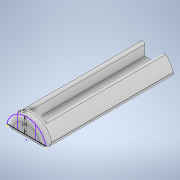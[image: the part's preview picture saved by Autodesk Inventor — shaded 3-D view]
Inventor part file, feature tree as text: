
AUTODESK INVENTOR PART (.ipt)
format: ipt  version: 2020 (Build 240168000, 168)  size: 165,888 bytes
history: native  units: in
note: dims shown in document units (in); Inventor stores cm internally (conversion verified against a paired STEP export)
features: extrude x3, sketch x2, fillet x2
ambient origin geometry x8: Origin, YZ Plane, XZ Plane, XY Plane, X Axis, Y Axis, Z Axis, Center Point
bodies: Solid1 (feature_tree)
feature tree (7):
  extrude  "Extrusion1"  Depth=2.5591in
  sketch  "Sketch2"  dims[d2=0.0394in d3=0.0in d6=0.0394in d7=0.0in d8=0.1969in d9=0.0in d12=0.315in d13=0.1772in d14=0.1181in d15=0.0394in d16=0.0197in d17=0.0344in]
  extrude  "Extrusion2"  Depth=0.0394in TaperAngle=0.0deg
  extrude  "Extrusion3"  Depth=0.1969in TaperAngle=0.0deg
  fillet  "Fillet3"  Radius=0.315in
  fillet  "Fillet4"  Radius=0.1772in
  sketch  "Sketch1"  dims[d0=0.7874in d1=2.5591in]
